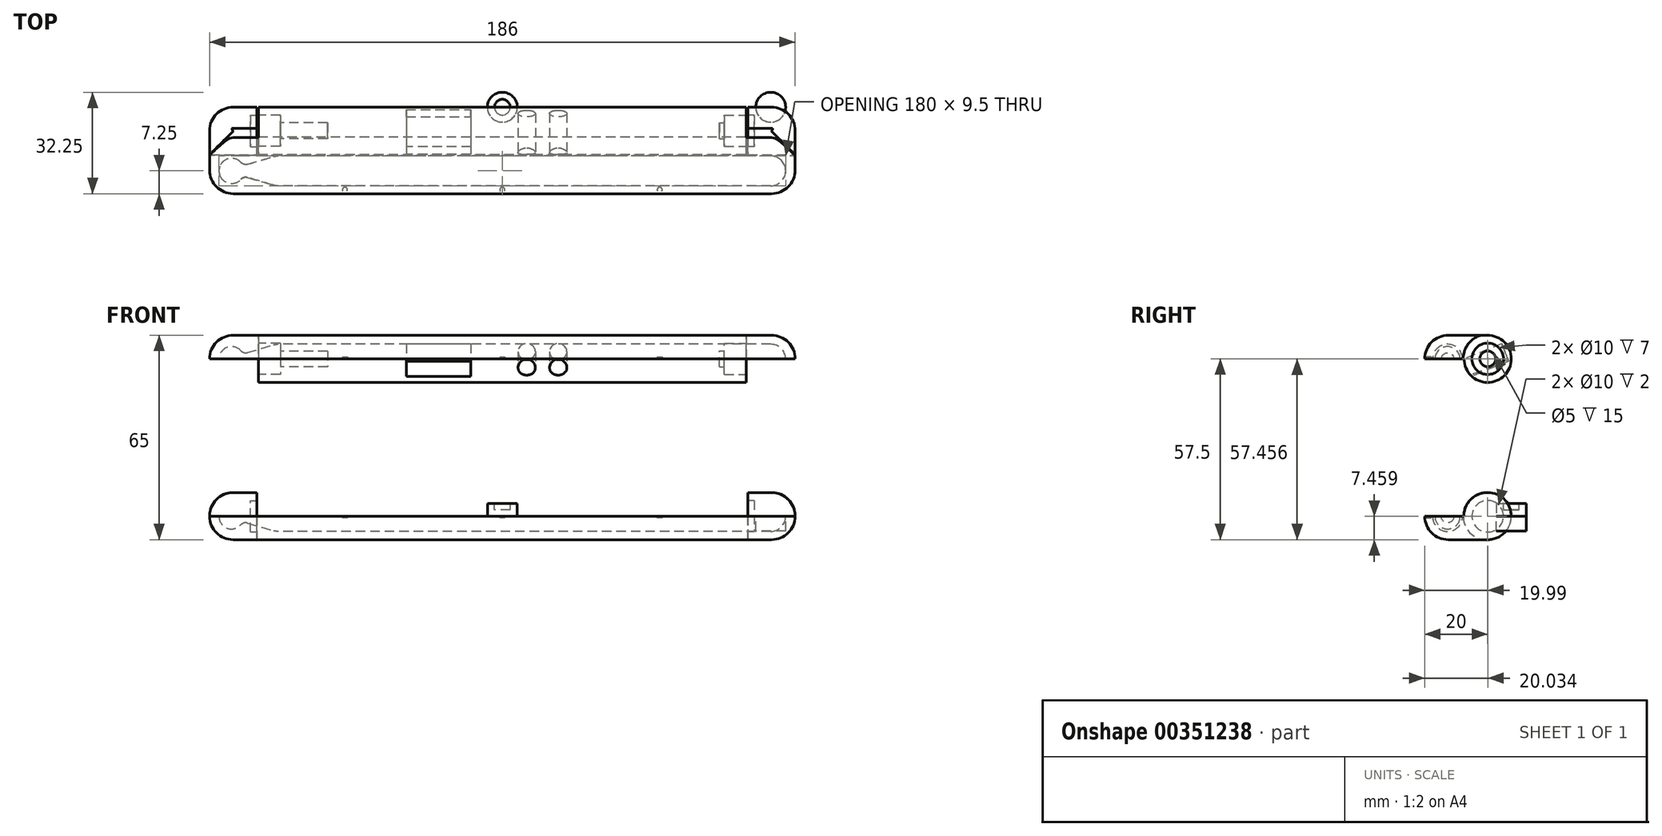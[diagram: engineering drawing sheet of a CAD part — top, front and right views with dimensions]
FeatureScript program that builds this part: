
annotation { "Feature Type Name" : "Feature", "Feature Type Description" : "" }
export const myFeature = defineFeature(function(context is Context, id is Id, definition is map)
    precondition{}
    {
        {
            var Q0;
            Q0=qCreatedBy(makeId("Front.planeOp"),FACE);
            var sketch = newSketch(context, id + "F0", { "sketchPlane" : qUnion([Q0])});
            skLineSegment(sketch, "E0.bottom", {"start": v(93, 7.5) * mm, "end": v(-93, 7.5) * mm});
            skLineSegment(sketch, "E0.top", {"start": v(93, -7.5) * mm, "end": v(-93, -7.5) * mm});
            skLineSegment(sketch, "E0.left", {"start": v(93, 7.5) * mm, "end": v(93, -7.5) * mm});
            skLineSegment(sketch, "E0.right", {"start": v(-93, 7.5) * mm, "end": v(-93, -7.5) * mm});
            skPoint(sketch, "E0.middle", {"position": v(0, 0) * mm});
            skSolve(sketch);
        }
        {
            var Q0;
            Q0=makeQuery(id+"F0.imprint","IMPRINT",FACE,{"disambiguationData":[TD([[makeQuery(id+"F0.imprint","IMPRINT",EDGE,{"derivedFrom":sQuery(id+"F0.wireOp",EDGE,"E0.bottom")}),1.0]])]});
            extrude(context, id + "F1", {"entities" : qUnion([Q0]), "depth" : 27.5 * mm});
        }
        {
            var Q0;
            Q0=makeQuery(id+"F1.opExtrude","CAP_EDGE",EDGE,{"disambiguationData":[OSD([sQuery(id+"F0.wireOp",EDGE,"E0.bottom")])],"isStart":false});
            var Q1;
            Q1=makeQuery(id+"F1.opExtrude","SWEPT_EDGE",EDGE,{"disambiguationData":[OSD([sQuery(id+"F0.wireOp",EDGE,"E0.bottom"),sQuery(id+"F0.wireOp",EDGE,"E0.left")])]});
            var Q2;
            Q2=makeQuery(id+"F1.opExtrude","CAP_EDGE",EDGE,{"disambiguationData":[OSD([sQuery(id+"F0.wireOp",EDGE,"E0.top")])],"isStart":false});
            var Q3;
            Q3=makeQuery(id+"F1.opExtrude","SWEPT_EDGE",EDGE,{"disambiguationData":[OSD([sQuery(id+"F0.wireOp",EDGE,"E0.top"),sQuery(id+"F0.wireOp",EDGE,"E0.left")])]});
            var Q4;
            Q4=makeQuery(id+"F1.opExtrude","CAP_EDGE",EDGE,{"disambiguationData":[OSD([sQuery(id+"F0.wireOp",EDGE,"E0.left")])],"isStart":false});
            var Q5;
            Q5=makeQuery(id+"F1.opExtrude","CAP_EDGE",EDGE,{"disambiguationData":[OSD([sQuery(id+"F0.wireOp",EDGE,"E0.bottom")])],"isStart":true});
            var Q6;
            Q6=makeQuery(id+"F1.opExtrude","CAP_EDGE",EDGE,{"disambiguationData":[OSD([sQuery(id+"F0.wireOp",EDGE,"E0.top")])],"isStart":true});
            var Q7;
            Q7=makeQuery(id+"F1.opExtrude","CAP_EDGE",EDGE,{"disambiguationData":[OSD([sQuery(id+"F0.wireOp",EDGE,"E0.left")])],"isStart":true});
            var Q8;
            Q8=makeQuery(id+"F1.opExtrude","CAP_EDGE",EDGE,{"disambiguationData":[OSD([sQuery(id+"F0.wireOp",EDGE,"E0.right")])],"isStart":true});
            var Q9;
            Q9=makeQuery(id+"F1.opExtrude","SWEPT_EDGE",EDGE,{"disambiguationData":[OSD([sQuery(id+"F0.wireOp",EDGE,"E0.bottom"),sQuery(id+"F0.wireOp",EDGE,"E0.right")])]});
            var Q10;
            Q10=makeQuery(id+"F1.opExtrude","SWEPT_EDGE",EDGE,{"disambiguationData":[OSD([sQuery(id+"F0.wireOp",EDGE,"E0.top"),sQuery(id+"F0.wireOp",EDGE,"E0.right")])]});
            var Q11;
            Q11=makeQuery(id+"F1.opExtrude","CAP_EDGE",EDGE,{"disambiguationData":[OSD([sQuery(id+"F0.wireOp",EDGE,"E0.right")])],"isStart":false});
            fillet(context, id + "F2", {"entities" : qUnion([Q0, Q1, Q2, Q3, Q4, Q5, Q6, Q7, Q8, Q9, Q10, Q11]), "radius" : 7.5 * mm, "tangentPropagation" : true, "allowEdgeOverflow" : false});
        }
        {
            var Q0;
            Q0=qCreatedBy(makeId("Right.planeOp"),FACE);
            cPlane(context, id + "F3", {"entities" : qUnion([Q0]), "cplaneType" : CPlaneType.OFFSET, "offset" : 78 * mm, "width" : 150 * mm, "height" : 150 * mm});
        }
        {
            var Q0;
            Q0=qCreatedBy(makeId("Front.planeOp"),FACE);
            var sketch = newSketch(context, id + "F4", { "sketchPlane" : qUnion([Q0])});
            skLineSegment(sketch, "E1", {"start": v(-72, 4.75) * mm, "end": v(85.25, 4.75) * mm});
            skLineSegment(sketch, "E2", {"start": v(-88, 0) * mm, "end": v(-72, 4.75) * mm});
            skArc(sketch, "E3", {"start": v(90, 0) * mm, "mid": v(88.6, 3.36) * mm, "end": v(85.25, 4.75) * mm});
            skLineSegment(sketch, "E4", {"start": v(-88, 0) * mm, "end": v(90, 0) * mm});
            skArc(sketch, "E5", {"start": v(-82, 0) * mm, "mid": v(-86, 4) * mm, "end": v(-90, 0) * mm});
            skLineSegment(sketch, "E6", {"start": v(-90, 0) * mm, "end": v(-82, 0) * mm});
            skSolve(sketch);
        }
        {
            var Q0;
            {var subQ0=sQuery(id+"F4.wireOp",EDGE,"E6");var subQ1=sQuery(id+"F4.wireOp",EDGE,"E2");var subQ2=makeQuery(id+"F4.imprint","INTERSECT",VERTEX,{"derivedFrom":[subQ1,subQ0]});Q0=makeQuery(id+"F4.imprint","IMPRINT",FACE,{"disambiguationData":[TD([[makeQuery(id+"F4.imprint","IMPRINT",EDGE,{"disambiguationData":[TD([[subQ2,-1.0]])],"derivedFrom":subQ1}),1.0]])]});}
            var Q1;
            {var subQ0=sQuery(id+"F4.wireOp",EDGE,"E6");var subQ1=sQuery(id+"F4.wireOp",EDGE,"E2");var subQ2=makeQuery(id+"F4.imprint","INTERSECT",VERTEX,{"derivedFrom":[subQ1,subQ0]});Q1=makeQuery(id+"F4.imprint","IMPRINT",FACE,{"disambiguationData":[TD([[makeQuery(id+"F4.imprint","IMPRINT",EDGE,{"disambiguationData":[TD([[subQ2,-1.0]])],"derivedFrom":subQ1}),-1.0]])]});}
            var Q2;
            {var subQ2=sQuery(id+"F4.wireOp",EDGE,"E1");Q2=makeQuery(id+"F4.imprint","IMPRINT",FACE,{"disambiguationData":[TD([[makeQuery(id+"F4.imprint","IMPRINT",EDGE,{"derivedFrom":subQ2}),-1.0]])]});}
            var Q3;
            Q3=sQuery(id+"F4.wireOp",EDGE,"E4");
            revolve(context, id + "F5", {"entities" : qUnion([Q0, Q1, Q2]), "axis" : qUnion([Q3]), "revolveType" : RevolveType.FULL});
        }
        {
            var Q0;
            Q0=makeQuery(id+"F5.opRevolve","SWEPT_EDGE",EDGE,{"disambiguationData":[OSD([sQuery(id+"F4.wireOp",EDGE,"E2"),sQuery(id+"F4.wireOp",EDGE,"E5")])]});
            fillet(context, id + "F6", {"entities" : qUnion([Q0]), "radius" : 2 * mm, "tangentPropagation" : true, "allowEdgeOverflow" : false});
        }
        {
            var Q0;
            Q0=makeQuery(id+"F5.opRevolve","SWEPT_EDGE",EDGE,{"disambiguationData":[OSD([sQuery(id+"F4.wireOp",EDGE,"E1"),sQuery(id+"F4.wireOp",EDGE,"E2")])]});
            fillet(context, id + "F7", {"entities" : qUnion([Q0]), "radius" : 5 * mm, "tangentPropagation" : true, "allowEdgeOverflow" : false});
        }
        {
            var Q0;
            Q0=qCreatedBy(makeId("Top.planeOp"),FACE);
            var sketch = newSketch(context, id + "F8", { "sketchPlane" : qUnion([Q0])});
            skCircle(sketch, "E7", {"center": v(85.25, 0) * mm, "radius": 4.75 * mm});
            skSolve(sketch);
        }
        {
            var Q0;
            Q0=makeQuery(id+"F8.imprint","IMPRINT",FACE,{"disambiguationData":[TD([[makeQuery(id+"F8.imprint","IMPRINT",EDGE,{"derivedFrom":sQuery(id+"F8.wireOp",EDGE,"E7")}),1.0]])]});
            extrude(context, id + "F9", {"entities" : qUnion([Q0]), "oppositeDirection" : true, "depth" : 4.75 * mm});
        }
        {
            var Q0;
            Q0=makeQuery(id+"F5.opRevolve","SWEPT_BODY",BODY,{"disambiguationData":[OSD([sQuery(id+"F4.wireOp",EDGE,"E1"),sQuery(id+"F4.wireOp",EDGE,"E2"),sQuery(id+"F4.wireOp",EDGE,"E3"),sQuery(id+"F4.wireOp",EDGE,"E4"),sQuery(id+"F4.wireOp",EDGE,"E5"),sQuery(id+"F4.wireOp",EDGE,"E6")])]});
            transform(context, id + "F10", {"entities" : qUnion([Q0]), "transformType" : TransformType.TRANSLATION_3D, "dx" : 0 * mm, "dy" : -20.25 * mm, "dz" : -0.1 * mm, "makeCopy" : false});
        }
        {
            var Q0;
            Q0=makeQuery(id+"F5.opRevolve","SWEPT_BODY",BODY,{"disambiguationData":[OSD([sQuery(id+"F4.wireOp",EDGE,"E1"),sQuery(id+"F4.wireOp",EDGE,"E2"),sQuery(id+"F4.wireOp",EDGE,"E3"),sQuery(id+"F4.wireOp",EDGE,"E4"),sQuery(id+"F4.wireOp",EDGE,"E5"),sQuery(id+"F4.wireOp",EDGE,"E6")])]});
            var Q1;
            Q1=makeQuery(id+"F1.opExtrude","SWEPT_BODY",BODY,{"disambiguationData":[OSD([sQuery(id+"F0.wireOp",EDGE,"E0.bottom"),sQuery(id+"F0.wireOp",EDGE,"E0.top"),sQuery(id+"F0.wireOp",EDGE,"E0.left"),sQuery(id+"F0.wireOp",EDGE,"E0.right")])]});
            booleanBodies(context, id + "F11", {"operationType" : BooleanOperationType.SUBTRACTION, "tools" : qUnion([Q0]), "targets" : qUnion([Q1]), "keepTools" : true});
        }
        {
            var Q0;
            Q0=makeQuery(id+"F1.opExtrude","SWEPT_BODY",BODY,{"disambiguationData":[OSD([sQuery(id+"F0.wireOp",EDGE,"E0.bottom"),sQuery(id+"F0.wireOp",EDGE,"E0.top"),sQuery(id+"F0.wireOp",EDGE,"E0.left"),sQuery(id+"F0.wireOp",EDGE,"E0.right")])]});
            transform(context, id + "F12", {"entities" : qUnion([Q0]), "transformType" : TransformType.TRANSLATION_3D, "dx" : 0 * mm, "dy" : 0 * mm, "dz" : 50 * mm, "makeCopy" : true});
        }
        {
            var Q0;
            Q0=qCreatedBy(makeId("Right.planeOp"),FACE);
            cPlane(context, id + "F13", {"entities" : qUnion([Q0]), "cplaneType" : CPlaneType.OFFSET, "offset" : 93 * mm, "width" : 150 * mm, "height" : 150 * mm});
        }
        {
            var Q0;
            Q0=qCreatedBy(makeId("Right.planeOp"),FACE);
            cPlane(context, id + "F14", {"entities" : qUnion([Q0]), "cplaneType" : CPlaneType.OFFSET, "offset" : 93 * mm, "oppositeDirection" : true, "width" : 150 * mm, "height" : 150 * mm});
        }
        {
            var Q0;
            Q0=qCreatedBy(id+"F13.planeOp",FACE);
            var sketch = newSketch(context, id + "F15", { "sketchPlane" : qUnion([Q0])});
            skCircle(sketch, "E8", {"center": v(-7.6, 0) * mm, "radius": 7.5 * mm});
            skLineSegment(sketch, "E9.bottom", {"start": v(-6.72, 0) * mm, "end": v(-52.07, 0) * mm});
            skLineSegment(sketch, "E9.top", {"start": v(-6.72, 20.65) * mm, "end": v(-52.07, 20.65) * mm});
            skLineSegment(sketch, "E9.left", {"start": v(-6.72, 0) * mm, "end": v(-6.72, 20.65) * mm});
            skLineSegment(sketch, "E9.right", {"start": v(-52.07, 0) * mm, "end": v(-52.07, 20.65) * mm});
            skPoint(sketch, "E9.middle", {"position": v(-29.4, 10.33) * mm});
            skSolve(sketch);
        }
        {
            var Q0;
            {var subQ1=sQuery(id+"F15.wireOp",EDGE,"E9.top");Q0=makeQuery(id+"F15.imprint","IMPRINT",FACE,{"disambiguationData":[TD([[makeQuery(id+"F15.imprint","IMPRINT",EDGE,{"derivedFrom":subQ1}),1.0]])]});}
            extrude(context, id + "F16", {"entities" : qUnion([Q0]), "operationType" : NewBodyOperationType.REMOVE, "endBound" : BoundingType.THROUGH_ALL, "oppositeDirection" : true, "depth" : 25 * mm});
        }
        {
            var Q0;
            Q0=qCreatedBy(id+"F13.planeOp",FACE);
            var sketch = newSketch(context, id + "F17", { "sketchPlane" : qUnion([Q0])});
            skCircle(sketch, "E10", {"center": v(-7.5, 50) * mm, "radius": 7.5 * mm});
            skLineSegment(sketch, "E11.bottom", {"start": v(-7.5, 50) * mm, "end": v(-34.83, 50) * mm});
            skLineSegment(sketch, "E11.top", {"start": v(-7.5, 41.08) * mm, "end": v(-34.83, 41.08) * mm});
            skLineSegment(sketch, "E11.left", {"start": v(-7.5, 50) * mm, "end": v(-7.5, 41.08) * mm});
            skLineSegment(sketch, "E11.right", {"start": v(-34.83, 50) * mm, "end": v(-34.83, 41.08) * mm});
            skSolve(sketch);
        }
        {
            var Q0;
            {var subQ1=sQuery(id+"F17.wireOp",EDGE,"E11.top");Q0=makeQuery(id+"F17.imprint","IMPRINT",FACE,{"disambiguationData":[TD([[makeQuery(id+"F17.imprint","IMPRINT",EDGE,{"derivedFrom":subQ1}),-1.0]])]});}
            extrude(context, id + "F18", {"entities" : qUnion([Q0]), "operationType" : NewBodyOperationType.REMOVE, "endBound" : BoundingType.THROUGH_ALL, "oppositeDirection" : true, "depth" : 25 * mm});
        }
        {
            var Q0;
            Q0=qCreatedBy(id+"F13.planeOp",FACE);
            var sketch = newSketch(context, id + "F19", { "sketchPlane" : qUnion([Q0])});
            skCircle(sketch, "E12", {"center": v(-7.5, 50) * mm, "radius": 7.8 * mm});
            skSolve(sketch);
        }
        {
            var Q0;
            Q0=makeQuery(id+"F19.imprint","IMPRINT",FACE,{"disambiguationData":[TD([[makeQuery(id+"F19.imprint","IMPRINT",EDGE,{"derivedFrom":sQuery(id+"F19.wireOp",EDGE,"E12")}),1.0]])]});
            extrude(context, id + "F20", {"entities" : qUnion([Q0]), "operationType" : NewBodyOperationType.REMOVE, "oppositeDirection" : true, "depth" : 15.5 * mm});
        }
        {
            var Q0;
            Q0=qCreatedBy(id+"F14.planeOp",FACE);
            var sketch = newSketch(context, id + "F21", { "sketchPlane" : qUnion([Q0])});
            skCircle(sketch, "E13", {"center": v(-7.5, 50) * mm, "radius": 7.8 * mm});
            skSolve(sketch);
        }
        {
            var Q0;
            Q0=makeQuery(id+"F21.imprint","IMPRINT",FACE,{"disambiguationData":[TD([[makeQuery(id+"F21.imprint","IMPRINT",EDGE,{"derivedFrom":sQuery(id+"F21.wireOp",EDGE,"E13")}),1.0]])]});
            extrude(context, id + "F22", {"entities" : qUnion([Q0]), "operationType" : NewBodyOperationType.REMOVE, "depth" : 15.5 * mm});
        }
        {
            var Q0;
            Q0=qCreatedBy(id+"F3.planeOp",FACE);
            var sketch = newSketch(context, id + "F23", { "sketchPlane" : qUnion([Q0])});
            skCircle(sketch, "E14", {"center": v(-7.5, 0) * mm, "radius": 7.75 * mm});
            skSolve(sketch);
        }
        {
            var Q0;
            Q0=makeQuery(id+"F23.imprint","IMPRINT",FACE,{"disambiguationData":[TD([[makeQuery(id+"F23.imprint","IMPRINT",EDGE,{"derivedFrom":sQuery(id+"F23.wireOp",EDGE,"E14")}),1.0]])]});
            extrude(context, id + "F24", {"entities" : qUnion([Q0]), "oppositeDirection" : true, "depth" : 156 * mm});
        }
        {
            var Q0;
            Q0=makeQuery(id+"F24.opExtrude","SWEPT_BODY",BODY,{"disambiguationData":[OSD([sQuery(id+"F23.wireOp",EDGE,"E14")])]});
            var Q1;
            Q1=makeQuery(id+"F1.opExtrude","SWEPT_BODY",BODY,{"disambiguationData":[OSD([sQuery(id+"F0.wireOp",EDGE,"E0.bottom"),sQuery(id+"F0.wireOp",EDGE,"E0.top"),sQuery(id+"F0.wireOp",EDGE,"E0.left"),sQuery(id+"F0.wireOp",EDGE,"E0.right")])]});
            booleanBodies(context, id + "F25", {"operationType" : BooleanOperationType.SUBTRACTION, "tools" : qUnion([Q0]), "targets" : qUnion([Q1])});
        }
        {
            var Q0;
            Q0=qCreatedBy(makeId("Front.planeOp"),FACE);
            cPlane(context, id + "F26", {"entities" : qUnion([Q0]), "cplaneType" : CPlaneType.OFFSET, "offset" : 16 * mm, "width" : 150 * mm, "height" : 150 * mm});
        }
        {
            var Q0;
            Q0=qCreatedBy(id+"F26.planeOp",FACE);
            var sketch = newSketch(context, id + "F27", { "sketchPlane" : qUnion([Q0])});
            skLineSegment(sketch, "E15.bottom", {"start": v(-30.5, 50) * mm, "end": v(-10, 50) * mm});
            skLineSegment(sketch, "E15.top", {"start": v(-30.5, 44) * mm, "end": v(-10, 44) * mm});
            skLineSegment(sketch, "E15.left", {"start": v(-30.5, 50) * mm, "end": v(-30.5, 44) * mm});
            skLineSegment(sketch, "E15.right", {"start": v(-10, 50) * mm, "end": v(-10, 44) * mm});
            skCircle(sketch, "E16", {"center": v(7.75, 47.25) * mm, "radius": 2.75 * mm});
            skCircle(sketch, "E17", {"center": v(17.75, 47.25) * mm, "radius": 2.75 * mm});
            skSolve(sketch);
        }
        {
            var Q0;
            Q0=makeQuery(id+"F27.imprint","IMPRINT",FACE,{"disambiguationData":[TD([[makeQuery(id+"F27.imprint","IMPRINT",EDGE,{"derivedFrom":sQuery(id+"F27.wireOp",EDGE,"E15.bottom")}),-1.0]])]});
            var Q1;
            Q1=makeQuery(id+"F27.imprint","IMPRINT",FACE,{"disambiguationData":[TD([[makeQuery(id+"F27.imprint","IMPRINT",EDGE,{"derivedFrom":sQuery(id+"F27.wireOp",EDGE,"E16")}),1.0]])]});
            var Q2;
            Q2=makeQuery(id+"F27.imprint","IMPRINT",FACE,{"disambiguationData":[TD([[makeQuery(id+"F27.imprint","IMPRINT",EDGE,{"derivedFrom":sQuery(id+"F27.wireOp",EDGE,"E17")}),1.0]])]});
            extrude(context, id + "F28", {"entities" : qUnion([Q0, Q1, Q2]), "oppositeDirection" : true, "depth" : 14 * mm});
        }
        {
            var Q0;
            Q0=makeQuery(id+"F28.opExtrude","SWEPT_BODY",BODY,{"disambiguationData":[OSD([sQuery(id+"F27.wireOp",EDGE,"E15.bottom"),sQuery(id+"F27.wireOp",EDGE,"E15.top"),sQuery(id+"F27.wireOp",EDGE,"E15.left"),sQuery(id+"F27.wireOp",EDGE,"E15.right")])]});
            var Q1;
            Q1=makeQuery(id+"F28.opExtrude","SWEPT_BODY",BODY,{"disambiguationData":[OSD([sQuery(id+"F27.wireOp",EDGE,"E16")])]});
            var Q2;
            Q2=makeQuery(id+"F28.opExtrude","SWEPT_BODY",BODY,{"disambiguationData":[OSD([sQuery(id+"F27.wireOp",EDGE,"E17")])]});
            var Q3;
            Q3=makeQuery(id+"F28.opExtrude","CAP_EDGE",EDGE,{"disambiguationData":[OSD([sQuery(id+"F27.wireOp",EDGE,"E15.bottom")])],"isStart":true});
            transform(context, id + "F29", {"entities" : qUnion([Q0, Q1, Q2]), "transformType" : TransformType.ROTATION, "transformAxis" : qUnion([Q3]), "angle" : 22.33 * degree, "makeCopy" : false});
        }
        {
            var Q0;
            Q0=makeQuery(id+"F28.opExtrude","SWEPT_BODY",BODY,{"disambiguationData":[OSD([sQuery(id+"F27.wireOp",EDGE,"E15.bottom"),sQuery(id+"F27.wireOp",EDGE,"E15.top"),sQuery(id+"F27.wireOp",EDGE,"E15.left"),sQuery(id+"F27.wireOp",EDGE,"E15.right")])]});
            transform(context, id + "F30", {"entities" : qUnion([Q0]), "transformType" : TransformType.TRANSLATION_3D, "dx" : 0 * mm, "dy" : 0 * mm, "dz" : -0.5 * mm, "makeCopy" : false});
        }
        {
            var Q0;
            Q0=makeQuery(id+"F28.opExtrude","SWEPT_BODY",BODY,{"disambiguationData":[OSD([sQuery(id+"F27.wireOp",EDGE,"E16")])]});
            transform(context, id + "F31", {"entities" : qUnion([Q0]), "transformType" : TransformType.TRANSLATION_3D, "dx" : 0 * mm, "dy" : 0 * mm, "dz" : -0.5 * mm, "makeCopy" : false});
        }
        {
            var Q0;
            Q0=makeQuery(id+"F28.opExtrude","SWEPT_BODY",BODY,{"disambiguationData":[OSD([sQuery(id+"F27.wireOp",EDGE,"E17")])]});
            transform(context, id + "F32", {"entities" : qUnion([Q0]), "transformType" : TransformType.TRANSLATION_3D, "dx" : 0 * mm, "dy" : 0 * mm, "dz" : -0.5 * mm, "makeCopy" : false});
        }
        {
            var Q0;
            Q0=makeQuery(id+"F28.opExtrude","SWEPT_BODY",BODY,{"disambiguationData":[OSD([sQuery(id+"F27.wireOp",EDGE,"E15.bottom"),sQuery(id+"F27.wireOp",EDGE,"E15.top"),sQuery(id+"F27.wireOp",EDGE,"E15.left"),sQuery(id+"F27.wireOp",EDGE,"E15.right")])]});
            var Q1;
            Q1=makeQuery(id+"F28.opExtrude","SWEPT_BODY",BODY,{"disambiguationData":[OSD([sQuery(id+"F27.wireOp",EDGE,"E16")])]});
            var Q2;
            Q2=makeQuery(id+"F28.opExtrude","SWEPT_BODY",BODY,{"disambiguationData":[OSD([sQuery(id+"F27.wireOp",EDGE,"E17")])]});
            var Q3;
            Q3=makeQuery(id+"F12.opPattern","COPY",BODY,{"derivedFrom":makeQuery(id+"F1.opExtrude","SWEPT_BODY",BODY,{"disambiguationData":[OSD([sQuery(id+"F0.wireOp",EDGE,"E0.bottom"),sQuery(id+"F0.wireOp",EDGE,"E0.top"),sQuery(id+"F0.wireOp",EDGE,"E0.left"),sQuery(id+"F0.wireOp",EDGE,"E0.right")])]}),"instanceName":"1"});
            booleanBodies(context, id + "F33", {"operationType" : BooleanOperationType.SUBTRACTION, "tools" : qUnion([Q0, Q1, Q2]), "targets" : qUnion([Q3])});
        }
        {
            var Q0;
            Q0=makeQuery(id+"F25.opBoolean","COPY",FACE,{"derivedFrom":makeQuery(id+"F24.opExtrude","CAP_FACE",FACE,{"disambiguationData":[OSD([sQuery(id+"F23.wireOp",EDGE,"E14")])],"isStart":false})});
            var sketch = newSketch(context, id + "F34", { "sketchPlane" : qUnion([Q0])});
            skCircle(sketch, "E18", {"center": v(-7.51, -0.04) * mm, "radius": 5 * mm});
            skSolve(sketch);
        }
        {
            var Q0;
            Q0=makeQuery(id+"F34.imprint","IMPRINT",FACE,{"disambiguationData":[TD([[makeQuery(id+"F34.imprint","IMPRINT",EDGE,{"derivedFrom":sQuery(id+"F34.wireOp",EDGE,"E18")}),1.0]])]});
            extrude(context, id + "F35", {"entities" : qUnion([Q0]), "operationType" : NewBodyOperationType.REMOVE, "oppositeDirection" : true, "depth" : 2 * mm});
        }
        {
            var Q0;
            Q0=makeQuery(id+"F20.boolean.opBoolean","COPY",FACE,{"derivedFrom":makeQuery(id+"F20.opExtrude","CAP_FACE",FACE,{"disambiguationData":[OSD([sQuery(id+"F19.wireOp",EDGE,"E12")])],"isStart":false})});
            var sketch = newSketch(context, id + "F36", { "sketchPlane" : qUnion([Q0])});
            skCircle(sketch, "E19", {"center": v(-7.5, 50) * mm, "radius": 5 * mm});
            skSolve(sketch);
        }
        {
            var Q0;
            Q0=makeQuery(id+"F36.imprint","IMPRINT",FACE,{"disambiguationData":[TD([[makeQuery(id+"F36.imprint","IMPRINT",EDGE,{"derivedFrom":sQuery(id+"F36.wireOp",EDGE,"E19")}),1.0]])]});
            extrude(context, id + "F37", {"entities" : qUnion([Q0]), "operationType" : NewBodyOperationType.REMOVE, "oppositeDirection" : true, "depth" : 7 * mm});
        }
        {
            var Q0;
            Q0=makeQuery(id+"F22.boolean.opBoolean","COPY",FACE,{"derivedFrom":makeQuery(id+"F22.opExtrude","CAP_FACE",FACE,{"disambiguationData":[OSD([sQuery(id+"F21.wireOp",EDGE,"E13")])],"isStart":false})});
            var sketch = newSketch(context, id + "F38", { "sketchPlane" : qUnion([Q0])});
            skCircle(sketch, "E20", {"center": v(7.5, 50) * mm, "radius": 5 * mm});
            skSolve(sketch);
        }
        {
            var Q0;
            Q0=makeQuery(id+"F38.imprint","IMPRINT",FACE,{"disambiguationData":[TD([[makeQuery(id+"F38.imprint","IMPRINT",EDGE,{"derivedFrom":sQuery(id+"F38.wireOp",EDGE,"E20")}),1.0]])]});
            extrude(context, id + "F39", {"entities" : qUnion([Q0]), "operationType" : NewBodyOperationType.REMOVE, "oppositeDirection" : true, "depth" : 7 * mm});
        }
        {
            var Q0;
            Q0=makeQuery(id+"F25.opBoolean","COPY",FACE,{"derivedFrom":makeQuery(id+"F24.opExtrude","CAP_FACE",FACE,{"disambiguationData":[OSD([sQuery(id+"F23.wireOp",EDGE,"E14")])],"isStart":true})});
            var sketch = newSketch(context, id + "F40", { "sketchPlane" : qUnion([Q0])});
            skCircle(sketch, "E21", {"center": v(7.51, -0.04) * mm, "radius": 5 * mm});
            skSolve(sketch);
        }
        {
            var Q0;
            Q0=makeQuery(id+"F40.imprint","IMPRINT",FACE,{"disambiguationData":[TD([[makeQuery(id+"F40.imprint","IMPRINT",EDGE,{"derivedFrom":sQuery(id+"F40.wireOp",EDGE,"E21")}),1.0]])]});
            extrude(context, id + "F41", {"entities" : qUnion([Q0]), "operationType" : NewBodyOperationType.REMOVE, "oppositeDirection" : true, "depth" : 2 * mm});
        }
        {
            var Q0;
            Q0=makeQuery(id+"F16.boolean.opBoolean","COPY",FACE,{"derivedFrom":makeQuery(id+"F16.opExtrude","SWEPT_FACE",FACE,{"disambiguationData":[OSD([sQuery(id+"F15.wireOp",EDGE,"E9.bottom")])]})});
            var sketch = newSketch(context, id + "F42", { "sketchPlane" : qUnion([Q0])});
            skCircle(sketch, "E22", {"center": v(0, -26.25) * mm, "radius": 0.8 * mm});
            skCircle(sketch, "E23", {"center": v(-50, -26.25) * mm, "radius": 0.8 * mm});
            skCircle(sketch, "E24", {"center": v(50, -26.25) * mm, "radius": 0.8 * mm});
            skSolve(sketch);
        }
        {
            var Q0;
            Q0=makeQuery(id+"F42.imprint","IMPRINT",FACE,{"disambiguationData":[TD([[makeQuery(id+"F42.imprint","IMPRINT",EDGE,{"derivedFrom":sQuery(id+"F42.wireOp",EDGE,"E24")}),1.0]])]});
            var Q1;
            Q1=makeQuery(id+"F42.imprint","IMPRINT",FACE,{"disambiguationData":[TD([[makeQuery(id+"F42.imprint","IMPRINT",EDGE,{"derivedFrom":sQuery(id+"F42.wireOp",EDGE,"E22")}),1.0]])]});
            var Q2;
            Q2=makeQuery(id+"F42.imprint","IMPRINT",FACE,{"disambiguationData":[TD([[makeQuery(id+"F42.imprint","IMPRINT",EDGE,{"derivedFrom":sQuery(id+"F42.wireOp",EDGE,"E23")}),1.0]])]});
            extrude(context, id + "F43", {"entities" : qUnion([Q0, Q1, Q2]), "operationType" : NewBodyOperationType.REMOVE, "oppositeDirection" : true, "depth" : 0.6 * mm});
        }
        {
            var Q0;
            Q0=makeQuery(id+"F18.boolean.opBoolean","COPY",FACE,{"derivedFrom":makeQuery(id+"F18.opExtrude","SWEPT_FACE",FACE,{"disambiguationData":[OSD([sQuery(id+"F17.wireOp",EDGE,"E11.bottom")])]})});
            var sketch = newSketch(context, id + "F44", { "sketchPlane" : qUnion([Q0])});
            skCircle(sketch, "E25", {"center": v(-50, 26.25) * mm, "radius": 0.8 * mm});
            skCircle(sketch, "E26", {"center": v(0, 26.25) * mm, "radius": 0.8 * mm});
            skCircle(sketch, "E27", {"center": v(50, 26.25) * mm, "radius": 0.8 * mm});
            skSolve(sketch);
        }
        {
            var Q0;
            Q0=makeQuery(id+"F44.imprint","IMPRINT",FACE,{"disambiguationData":[TD([[makeQuery(id+"F44.imprint","IMPRINT",EDGE,{"derivedFrom":sQuery(id+"F44.wireOp",EDGE,"E25")}),1.0]])]});
            var Q1;
            Q1=makeQuery(id+"F44.imprint","IMPRINT",FACE,{"disambiguationData":[TD([[makeQuery(id+"F44.imprint","IMPRINT",EDGE,{"derivedFrom":sQuery(id+"F44.wireOp",EDGE,"E26")}),1.0]])]});
            var Q2;
            Q2=makeQuery(id+"F44.imprint","IMPRINT",FACE,{"disambiguationData":[TD([[makeQuery(id+"F44.imprint","IMPRINT",EDGE,{"derivedFrom":sQuery(id+"F44.wireOp",EDGE,"E27")}),1.0]])]});
            extrude(context, id + "F45", {"entities" : qUnion([Q0, Q1, Q2]), "operationType" : NewBodyOperationType.REMOVE, "oppositeDirection" : true, "depth" : 0.6 * mm});
        }
        {
            var Q0;
            Q0=makeQuery(id+"F37.boolean.opBoolean","COPY",FACE,{"derivedFrom":makeQuery(id+"F37.opExtrude","CAP_FACE",FACE,{"disambiguationData":[OSD([sQuery(id+"F36.wireOp",EDGE,"E19")])],"isStart":false})});
            var sketch = newSketch(context, id + "F46", { "sketchPlane" : qUnion([Q0])});
            skCircle(sketch, "E28", {"center": v(-7.5, 50) * mm, "radius": 2.5 * mm});
            skSolve(sketch);
        }
        {
            var Q0;
            Q0=makeQuery(id+"F46.imprint","IMPRINT",FACE,{"disambiguationData":[TD([[makeQuery(id+"F46.imprint","IMPRINT",EDGE,{"derivedFrom":sQuery(id+"F46.wireOp",EDGE,"E28")}),1.0]])]});
            extrude(context, id + "F47", {"entities" : qUnion([Q0]), "operationType" : NewBodyOperationType.REMOVE, "oppositeDirection" : true, "depth" : 1.5 * mm});
        }
        {
            var Q0;
            Q0=makeQuery(id+"F38.imprint","IMPRINT",FACE,{"disambiguationData":[TD([[makeQuery(id+"F38.imprint","IMPRINT",EDGE,{"derivedFrom":sQuery(id+"F38.wireOp",EDGE,"E20")}),1.0]])]});
            var sketch = newSketch(context, id + "F48", { "sketchPlane" : qUnion([Q0])});
            skCircle(sketch, "E29", {"center": v(7.47, 49.96) * mm, "radius": 2.5 * mm});
            skSolve(sketch);
        }
        {
            var Q0;
            Q0=makeQuery(id+"F48.imprint","IMPRINT",FACE,{"disambiguationData":[TD([[makeQuery(id+"F48.imprint","IMPRINT",EDGE,{"derivedFrom":sQuery(id+"F48.wireOp",EDGE,"E29")}),1.0]])]});
            extrude(context, id + "F49", {"entities" : qUnion([Q0]), "operationType" : NewBodyOperationType.REMOVE, "oppositeDirection" : true, "depth" : 22 * mm});
        }
        {
            var Q0;
            Q0=qCreatedBy(makeId("Top.planeOp"),FACE);
            var sketch = newSketch(context, id + "F50", { "sketchPlane" : qUnion([Q0])});
            skCircle(sketch, "E30", {"center": v(0, 0) * mm, "radius": 4.75 * mm});
            skSolve(sketch);
        }
        {
            var Q0;
            Q0=makeQuery(id+"F50.imprint","IMPRINT",FACE,{"disambiguationData":[TD([[makeQuery(id+"F50.imprint","IMPRINT",EDGE,{"derivedFrom":sQuery(id+"F50.wireOp",EDGE,"E30")}),1.0]])]});
            extrude(context, id + "F51", {"entities" : qUnion([Q0]), "depth" : 4 * mm});
        }
        {
            var Q0;
            Q0=makeQuery(id+"F51.opExtrude","CAP_FACE",FACE,{"disambiguationData":[OSD([sQuery(id+"F50.wireOp",EDGE,"E30")])],"isStart":false});
            var sketch = newSketch(context, id + "F52", { "sketchPlane" : qUnion([Q0])});
            skCircle(sketch, "E31", {"center": v(0, 0) * mm, "radius": 2.5 * mm});
            skSolve(sketch);
        }
        {
            var Q0;
            Q0=makeQuery(id+"F52.imprint","IMPRINT",FACE,{"disambiguationData":[TD([[makeQuery(id+"F52.imprint","IMPRINT",EDGE,{"derivedFrom":sQuery(id+"F52.wireOp",EDGE,"E31")}),1.0]])]});
            extrude(context, id + "F53", {"entities" : qUnion([Q0]), "operationType" : NewBodyOperationType.REMOVE, "oppositeDirection" : true, "depth" : 2 * mm});
        }
    });
